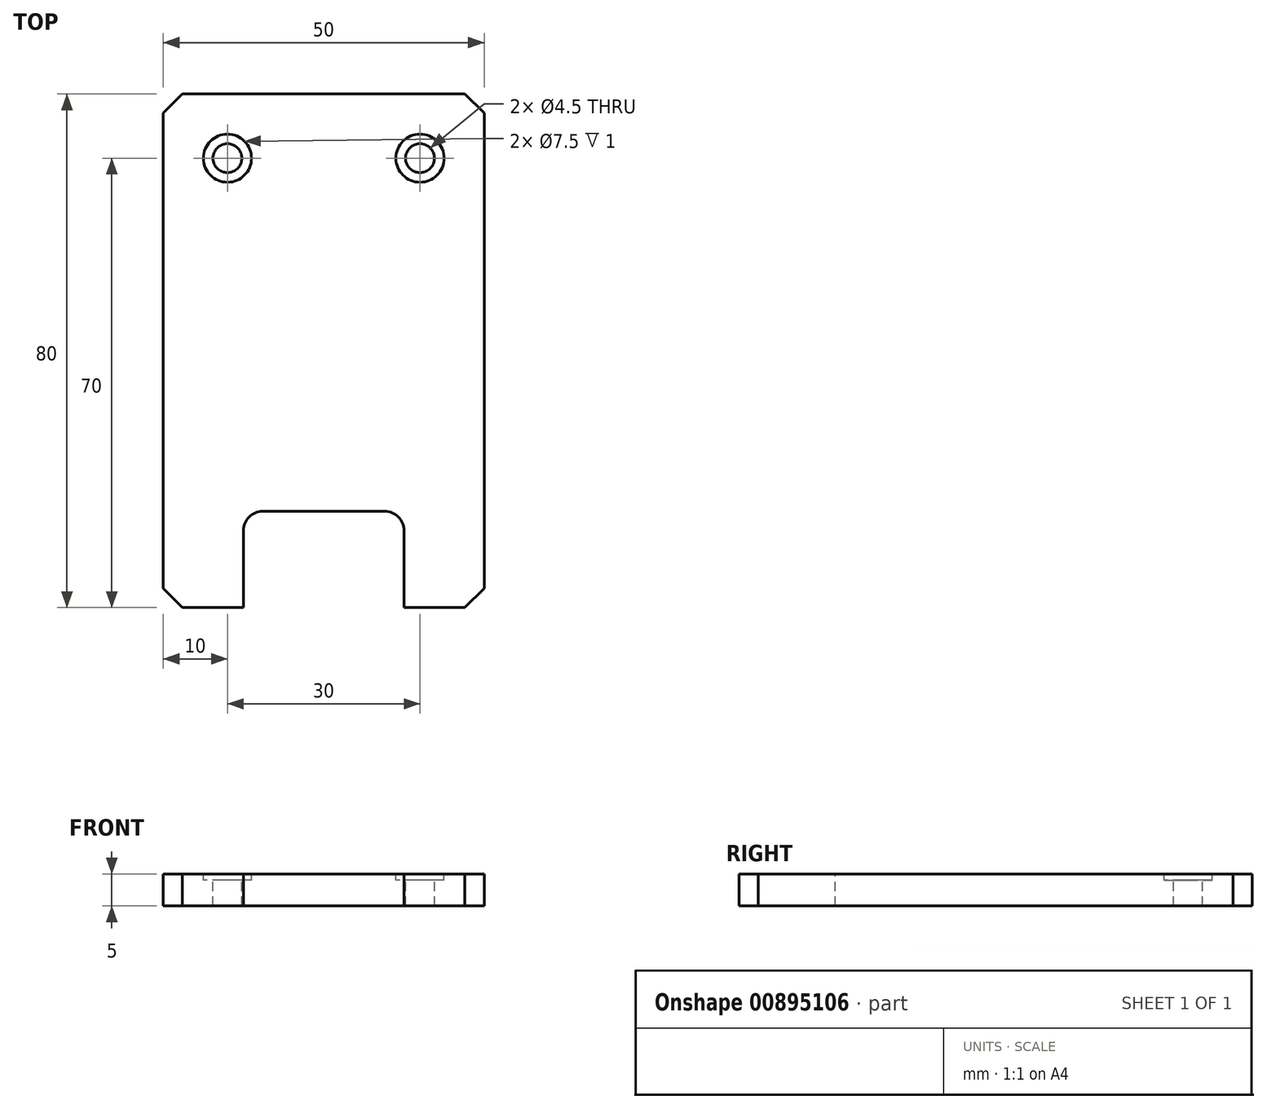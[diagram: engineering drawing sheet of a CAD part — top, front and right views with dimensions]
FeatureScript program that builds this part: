
annotation { "Feature Type Name" : "Feature", "Feature Type Description" : "" }
export const myFeature = defineFeature(function(context is Context, id is Id, definition is map)
    precondition{}
    {
        {
            var Q0;
            Q0=qCreatedBy(makeId("Top.planeOp"),FACE);
            var sketch = newSketch(context, id + "F0", { "sketchPlane" : qUnion([Q0])});
            skLineSegment(sketch, "E0.bottom", {"start": v(0, 0) * mm, "end": v(50, 0) * mm});
            skLineSegment(sketch, "E0.top", {"start": v(0, 80) * mm, "end": v(50, 80) * mm});
            skLineSegment(sketch, "E0.left", {"start": v(0, 0) * mm, "end": v(0, 80) * mm});
            skLineSegment(sketch, "E0.right", {"start": v(50, 0) * mm, "end": v(50, 80) * mm});
            skSolve(sketch);
        }
        {
            var Q0;
            Q0=makeQuery(id+"F0.imprint","IMPRINT",FACE,{"disambiguationData":[TD([[makeQuery(id+"F0.imprint","IMPRINT",EDGE,{"derivedFrom":sQuery(id+"F0.wireOp",EDGE,"E0.bottom")}),1.0]])]});
            extrude(context, id + "F1", {"entities" : qUnion([Q0]), "depth" : 5 * mm, "offsetDistance" : 25 * mm});
        }
        {
            var Q0;
            Q0=makeQuery(id+"F1.opExtrude","CAP_FACE",FACE,{"disambiguationData":[OSD([sQuery(id+"F0.wireOp",EDGE,"E0.bottom"),sQuery(id+"F0.wireOp",EDGE,"E0.top"),sQuery(id+"F0.wireOp",EDGE,"E0.left"),sQuery(id+"F0.wireOp",EDGE,"E0.right")])],"isStart":false});
            var sketch = newSketch(context, id + "F2", { "sketchPlane" : qUnion([Q0])});
            skLineSegment(sketch, "E1.bottom", {"start": v(12.5, 0) * mm, "end": v(37.5, 0) * mm});
            skLineSegment(sketch, "E1.top", {"start": v(12.5, 15) * mm, "end": v(37.5, 15) * mm});
            skLineSegment(sketch, "E1.left", {"start": v(12.5, 0) * mm, "end": v(12.5, 15) * mm});
            skLineSegment(sketch, "E1.right", {"start": v(37.5, 0) * mm, "end": v(37.5, 15) * mm});
            skSolve(sketch);
        }
        {
            var Q0;
            Q0=makeQuery(id+"F2.imprint","IMPRINT",FACE,{"disambiguationData":[TD([[makeQuery(id+"F2.imprint","IMPRINT",EDGE,{"derivedFrom":sQuery(id+"F2.wireOp",EDGE,"E1.bottom")}),1.0]])]});
            extrude(context, id + "F3", {"entities" : qUnion([Q0]), "operationType" : NewBodyOperationType.REMOVE, "oppositeDirection" : true, "depth" : 25 * mm, "offsetDistance" : 25 * mm});
        }
        {
            var Q0;
            Q0=makeQuery(id+"F3.boolean.opBoolean","COPY",EDGE,{"derivedFrom":makeQuery(id+"F3.opExtrude","SWEPT_EDGE",EDGE,{"disambiguationData":[OSD([sQuery(id+"F2.wireOp",EDGE,"E1.top"),sQuery(id+"F2.wireOp",EDGE,"E1.left")])]})});
            var Q1;
            Q1=makeQuery(id+"F3.boolean.opBoolean","COPY",EDGE,{"derivedFrom":makeQuery(id+"F3.opExtrude","SWEPT_EDGE",EDGE,{"disambiguationData":[OSD([sQuery(id+"F2.wireOp",EDGE,"E1.top"),sQuery(id+"F2.wireOp",EDGE,"E1.right")])]})});
            fillet(context, id + "F4", {"entities" : qUnion([Q0, Q1]), "radius" : 3 * mm, "tangentPropagation" : true, "allowEdgeOverflow" : false});
        }
        {
            var Q0;
            Q0=makeQuery(id+"F1.opExtrude","CAP_FACE",FACE,{"disambiguationData":[OSD([sQuery(id+"F0.wireOp",EDGE,"E0.bottom"),sQuery(id+"F0.wireOp",EDGE,"E0.top"),sQuery(id+"F0.wireOp",EDGE,"E0.left"),sQuery(id+"F0.wireOp",EDGE,"E0.right")])],"isStart":false});
            var sketch = newSketch(context, id + "F5", { "sketchPlane" : qUnion([Q0])});
            skCircle(sketch, "E2", {"center": v(10, 70) * mm, "radius": 3.75 * mm});
            skCircle(sketch, "E3", {"center": v(40, 70) * mm, "radius": 3.75 * mm});
            skSolve(sketch);
        }
        {
            var Q0;
            Q0=makeQuery(id+"F1.opExtrude","SWEPT_EDGE",EDGE,{"disambiguationData":[OSD([sQuery(id+"F0.wireOp",EDGE,"E0.top"),sQuery(id+"F0.wireOp",EDGE,"E0.left")])]});
            var Q1;
            Q1=makeQuery(id+"F1.opExtrude","SWEPT_EDGE",EDGE,{"disambiguationData":[OSD([sQuery(id+"F0.wireOp",EDGE,"E0.top"),sQuery(id+"F0.wireOp",EDGE,"E0.right")])]});
            var Q2;
            Q2=makeQuery(id+"F1.opExtrude","SWEPT_EDGE",EDGE,{"disambiguationData":[OSD([sQuery(id+"F0.wireOp",EDGE,"E0.bottom"),sQuery(id+"F0.wireOp",EDGE,"E0.left")])]});
            var Q3;
            Q3=makeQuery(id+"F1.opExtrude","SWEPT_EDGE",EDGE,{"disambiguationData":[OSD([sQuery(id+"F0.wireOp",EDGE,"E0.bottom"),sQuery(id+"F0.wireOp",EDGE,"E0.right")])]});
            chamfer(context, id + "F6", {"entities" : qUnion([Q0, Q1, Q2, Q3]), "width" : 3 * mm, "tangentPropagation" : true});
        }
        {
            var Q0;
            Q0=sQuery(id+"F5.wireOp",VERTEX,"E2.center");
            var Q1;
            Q1=sQuery(id+"F5.wireOp",VERTEX,"E3.center");
            var Q2;
            Q2=makeQuery(id+"F1.opExtrude","SWEPT_BODY",BODY,{"disambiguationData":[OSD([sQuery(id+"F0.wireOp",EDGE,"E0.bottom"),sQuery(id+"F0.wireOp",EDGE,"E0.top"),sQuery(id+"F0.wireOp",EDGE,"E0.left"),sQuery(id+"F0.wireOp",EDGE,"E0.right")])]});
            hole(context, id + "F7", {"style" : HoleStyle.SIMPLE, "endStyle" : HoleEndStyle.BLIND, "holeDiameter" : 4.5 * mm, "majorDiameter" : 5 * mm, "holeDepth" : 12 * mm, "isTappedThrough" : true, "tappedDepth" : 12 * mm, "tapClearance" : 3, "startFromSketch" : true, "locations" : qUnion([Q0, Q1]), "scope" : qUnion([Q2])});
        }
        {
            var Q0;
            Q0 = qSketchRegion(id + "F5", true);
            extrude(context, id + "F8", {"entities" : qUnion([Q0]), "operationType" : NewBodyOperationType.REMOVE, "oppositeDirection" : true, "depth" : 1 * mm, "offsetDistance" : 25 * mm});
        }
    });
